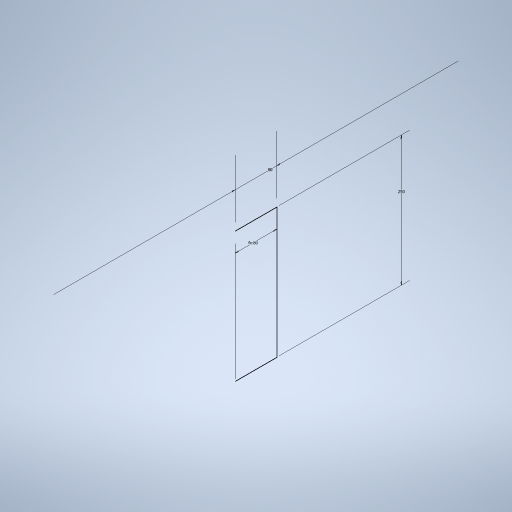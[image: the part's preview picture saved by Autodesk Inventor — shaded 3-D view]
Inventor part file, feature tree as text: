
AUTODESK INVENTOR PART (.ipt)
format: ipt  version: 2024.3 (Build 283343000, 343)  size: 231,936 bytes
history: native  units: mm
features: sketch x1
ambient origin geometry x8: Origin, YZ Plane, XZ Plane, XY Plane, X Axis, Y Axis, Z Axis, Center Point
feature tree (1):
  sketch  "Sketch1"  dims[d3=80.0mm d4=80.0mm d5=250.0mm]
